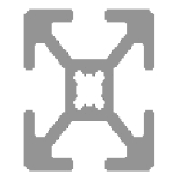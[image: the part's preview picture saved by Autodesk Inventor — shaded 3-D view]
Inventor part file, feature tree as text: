
AUTODESK INVENTOR PART (.ipt)
format: ipt  version: 2023.1 (Build 271208000, 208)  size: 236,032 bytes
history: native  units: in
note: dims shown in document units (in); Inventor stores cm internally (conversion verified against a paired STEP export)
features: other x4, sketch x3, plane x1
ambient origin geometry x8: Origin, YZ Plane, XZ Plane, XY Plane, X Axis, Y Axis, Z Axis, Center Point
bodies: Solid1 (feature_tree), Body (feature_tree)
feature tree (8):
  other  "Driven Length"
  other  "Blocks"
  other  "Start Plane"
  other  "End Plane"
  sketch  "Sketch1"  dims[d2=-0.0in]
  sketch  "Sketch2"  dims[d3=1.0in]
  plane  "Work Plane3"
  sketch  "Sketch3"  dims[d4=0.13in d5=0.0in d6=90.0deg d7=1.0in]
